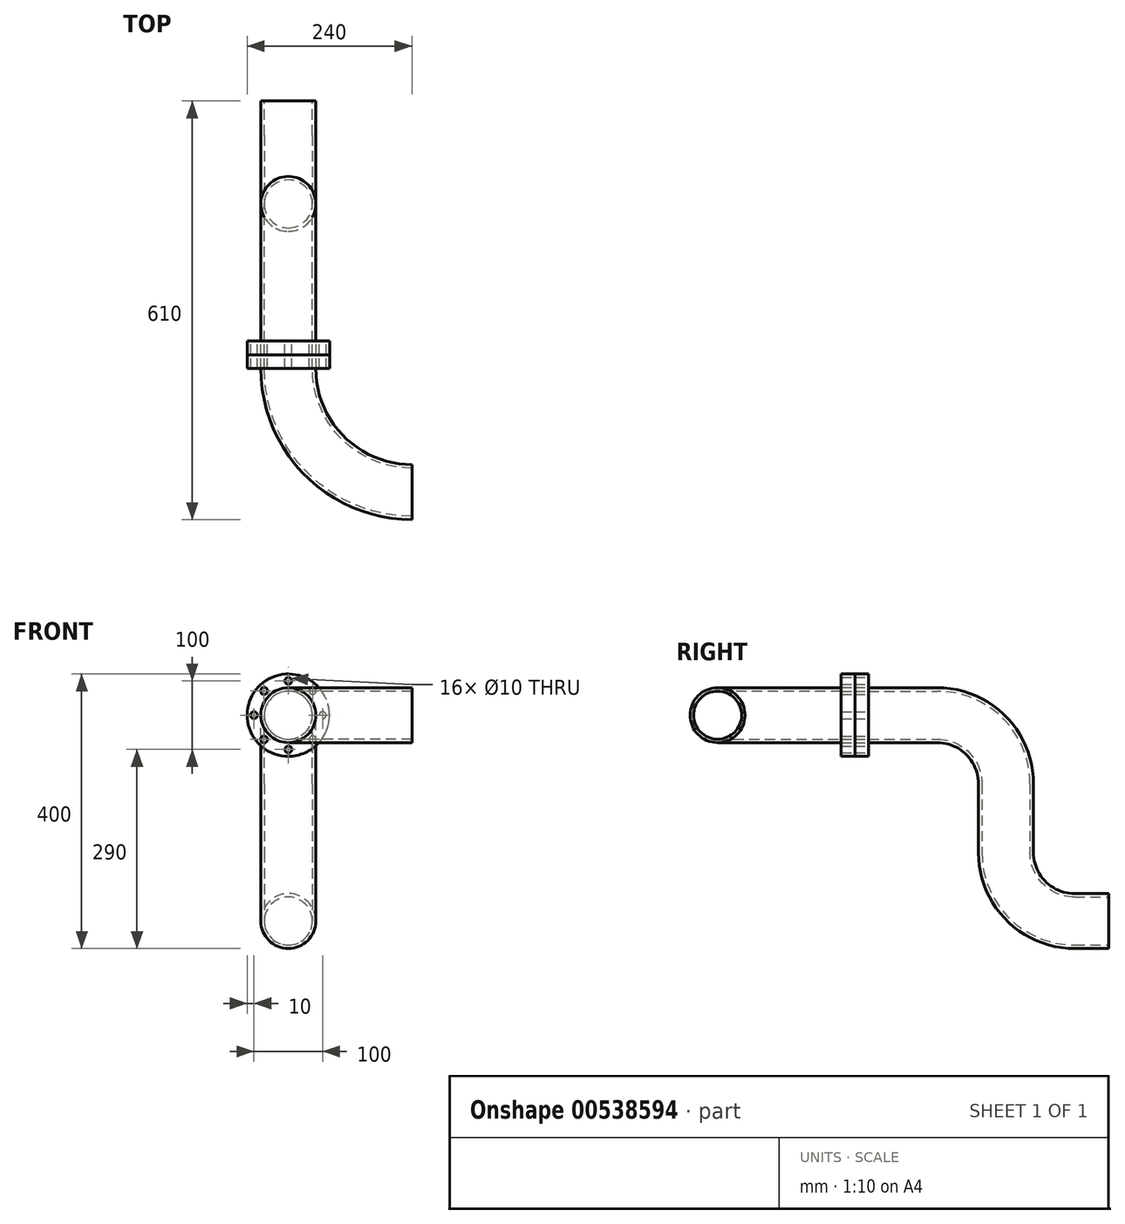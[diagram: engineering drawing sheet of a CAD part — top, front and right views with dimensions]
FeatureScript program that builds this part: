
annotation { "Feature Type Name" : "Feature", "Feature Type Description" : "" }
export const myFeature = defineFeature(function(context is Context, id is Id, definition is map)
    precondition{}
    {
        {
            var Q0;
            Q0=qCreatedBy(makeId("Front.planeOp"),FACE);
            var sketch = newSketch(context, id + "F0", { "sketchPlane" : qUnion([Q0])});
            skCircle(sketch, "E0", {"center": v(0, 0) * mm, "radius": 60 * mm});
            skCircle(sketch, "E1", {"center": v(0, 50) * mm, "radius": 5 * mm});
            skCircle(sketch, "E2.1.0", {"center": v(-35.36, 35.36) * mm, "radius": 5 * mm});
            skCircle(sketch, "E2.2.0", {"center": v(-50, 0) * mm, "radius": 5 * mm});
            skCircle(sketch, "E2.3.0", {"center": v(-35.36, -35.36) * mm, "radius": 5 * mm});
            skCircle(sketch, "E2.4.0", {"center": v(0, -50) * mm, "radius": 5 * mm});
            skCircle(sketch, "E2.5.0", {"center": v(35.36, -35.36) * mm, "radius": 5 * mm});
            skCircle(sketch, "E2.6.0", {"center": v(50, 0) * mm, "radius": 5 * mm});
            skCircle(sketch, "E2.7.0", {"center": v(35.36, 35.36) * mm, "radius": 5 * mm});
            skCircle(sketch, "E3", {"center": v(0, 0) * mm, "radius": 35 * mm});
            skSolve(sketch);
        }
        {
            var Q0;
            Q0 = qSketchRegion(id + "F0", true);
            extrude(context, id + "F1", {"entities" : qUnion([Q0]), "depth" : 20 * mm, "offsetDistance" : 25 * mm});
        }
        {
            var Q0;
            Q0=qCreatedBy(makeId("Front.planeOp"),FACE);
            var sketch = newSketch(context, id + "F2", { "sketchPlane" : qUnion([Q0])});
            skCircle(sketch, "E4", {"center": v(0, 0) * mm, "radius": 35 * mm});
            skCircle(sketch, "E5", {"center": v(0, 0) * mm, "radius": 40 * mm});
            skSolve(sketch);
        }
        {
            var Q0;
            Q0=qCreatedBy(makeId("Right.planeOp"),FACE);
            var sketch = newSketch(context, id + "F3", { "sketchPlane" : qUnion([Q0])});
            skLineSegment(sketch, "E6", {"start": v(0, 0) * mm, "end": v(100, 0) * mm});
            skLineSegment(sketch, "E7", {"start": v(200, -100) * mm, "end": v(200, -200) * mm});
            skLineSegment(sketch, "E8", {"start": v(300, -300) * mm, "end": v(350, -300) * mm});
            skPoint(sketch, "E9.visualSharp", {"position": v(200, 0) * mm});
            skArc(sketch, "E9.filletArc", {"start": v(200, -100) * mm, "mid": v(170.71, -29.29) * mm, "end": v(100, 0) * mm});
            skPoint(sketch, "E10.visualSharp", {"position": v(200, -300) * mm});
            skArc(sketch, "E10.filletArc", {"start": v(200, -200) * mm, "mid": v(229.29, -270.71) * mm, "end": v(300, -300) * mm});
            skSolve(sketch);
        }
        {
            var Q0;
            Q0=makeQuery(id+"F2.imprint","IMPRINT",FACE,{"disambiguationData":[TD([[makeQuery(id+"F2.imprint","IMPRINT",EDGE,{"derivedFrom":sQuery(id+"F2.wireOp",EDGE,"E4")}),-1.0]])]});
            var Q1;
            Q1=sQuery(id+"F3.wireOp",EDGE,"E6");
            var Q2;
            Q2=sQuery(id+"F3.wireOp",EDGE,"E9.filletArc");
            var Q3;
            Q3=sQuery(id+"F3.wireOp",EDGE,"E7");
            var Q4;
            Q4=sQuery(id+"F3.wireOp",EDGE,"E10.filletArc");
            var Q5;
            Q5=sQuery(id+"F3.wireOp",EDGE,"E8");
            sweep(context, id + "F4", {"profiles" : qUnion([Q0]), "path" : qUnion([Q1, Q2, Q3, Q4, Q5])});
        }
        {
            var Q0;
            Q0=makeQuery(id+"F1.opExtrude","CAP_FACE",FACE,{"disambiguationData":[OSD([sQuery(id+"F0.wireOp",EDGE,"E0"),sQuery(id+"F0.wireOp",EDGE,"E1"),sQuery(id+"F0.wireOp",EDGE,"E2.1.0"),sQuery(id+"F0.wireOp",EDGE,"E2.2.0"),sQuery(id+"F0.wireOp",EDGE,"E2.3.0"),sQuery(id+"F0.wireOp",EDGE,"E2.4.0"),sQuery(id+"F0.wireOp",EDGE,"E2.5.0"),sQuery(id+"F0.wireOp",EDGE,"E2.6.0"),sQuery(id+"F0.wireOp",EDGE,"E2.7.0"),sQuery(id+"F0.wireOp",EDGE,"E3")])],"isStart":false});
            extrude(context, id + "F5", {"entities" : qUnion([Q0]), "depth" : 20 * mm, "offsetDistance" : 25 * mm});
        }
        {
            var Q0;
            Q0=makeQuery(id+"F5.opExtrude","CAP_FACE",FACE,{"disambiguationData":[OSD([sQuery(id+"F0.wireOp",EDGE,"E0"),sQuery(id+"F0.wireOp",EDGE,"E1"),sQuery(id+"F0.wireOp",EDGE,"E2.1.0"),sQuery(id+"F0.wireOp",EDGE,"E2.2.0"),sQuery(id+"F0.wireOp",EDGE,"E2.3.0"),sQuery(id+"F0.wireOp",EDGE,"E2.4.0"),sQuery(id+"F0.wireOp",EDGE,"E2.5.0"),sQuery(id+"F0.wireOp",EDGE,"E2.6.0"),sQuery(id+"F0.wireOp",EDGE,"E2.7.0"),sQuery(id+"F0.wireOp",EDGE,"E3")])],"isStart":false});
            var sketch = newSketch(context, id + "F6", { "sketchPlane" : qUnion([Q0])});
            skCircle(sketch, "E11", {"center": v(0, 0) * mm, "radius": 35 * mm});
            skCircle(sketch, "E12", {"center": v(0, 0) * mm, "radius": 40 * mm});
            skLineSegment(sketch, "E13", {"start": v(180, 144.5) * mm, "end": v(180, -142.35) * mm, "construction": true});
            skSolve(sketch);
        }
        {
            var Q0;
            Q0=makeQuery(id+"F6.imprint","IMPRINT",FACE,{"disambiguationData":[TD([[makeQuery(id+"F6.imprint","IMPRINT",EDGE,{"derivedFrom":sQuery(id+"F6.wireOp",EDGE,"E11")}),-1.0]])]});
            var Q1;
            Q1=sQuery(id+"F6.wireOp",EDGE,"E13");
            revolve(context, id + "F7", {"operationType" : NewBodyOperationType.ADD, "entities" : qUnion([Q0]), "axis" : qUnion([Q1]), "revolveType" : RevolveType.ONE_DIRECTION, "oppositeDirection" : true, "angle" : 90 * degree});
        }
    });
